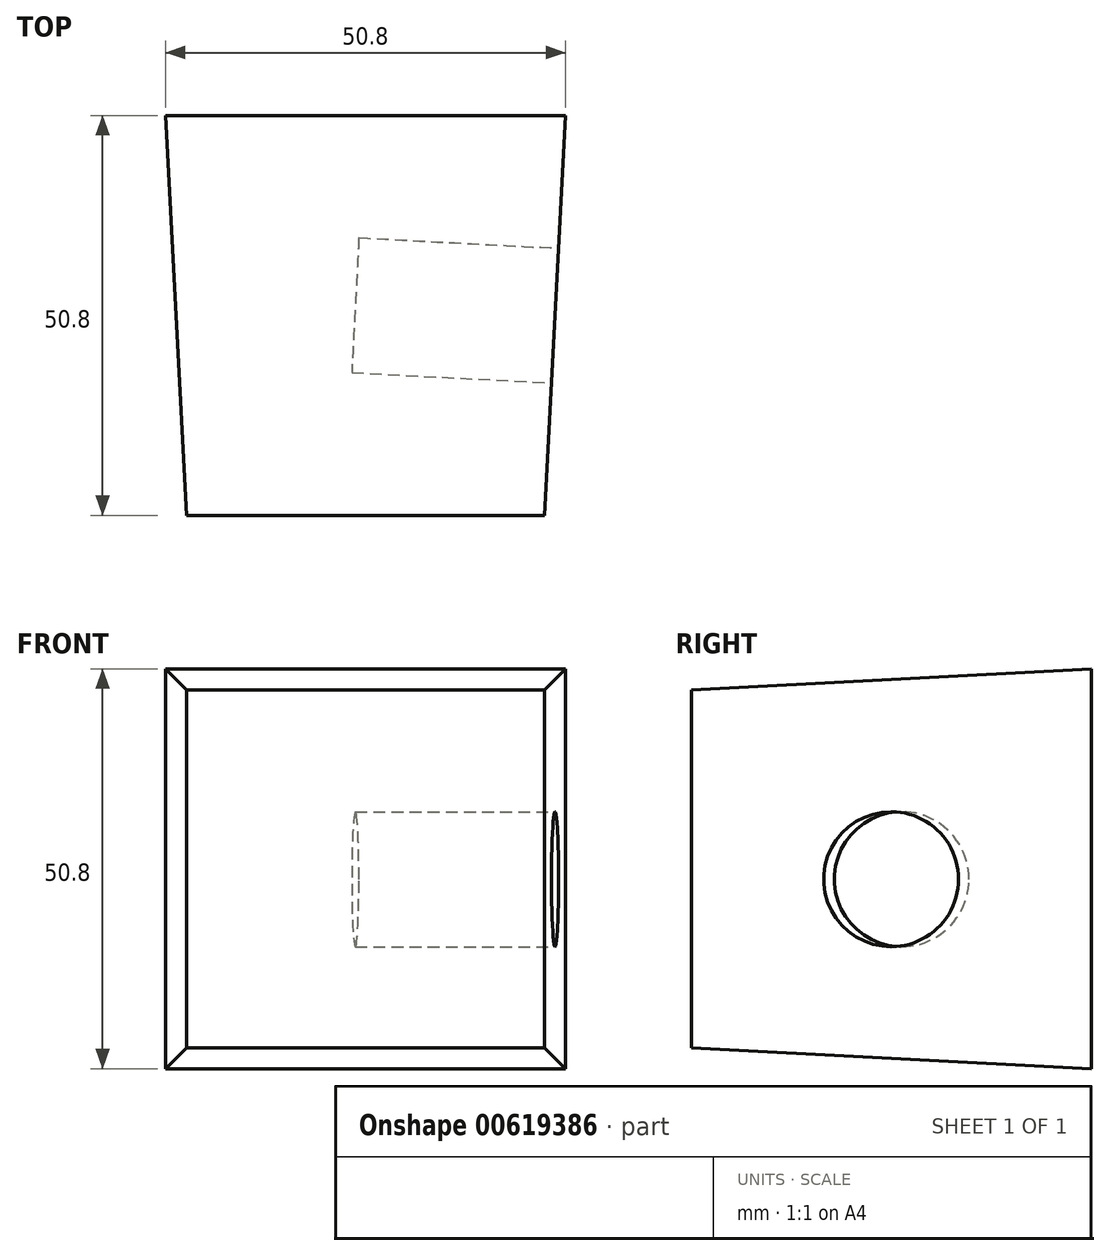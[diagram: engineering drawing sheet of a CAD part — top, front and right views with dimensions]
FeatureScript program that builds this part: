
annotation { "Feature Type Name" : "Feature", "Feature Type Description" : "" }
export const myFeature = defineFeature(function(context is Context, id is Id, definition is map)
    precondition{}
    {
        {
            var Q0;
            Q0=qCreatedBy(makeId("Front.planeOp"),FACE);
            var sketch = newSketch(context, id + "F0", { "sketchPlane" : qUnion([Q0])});
            skLineSegment(sketch, "E0", {"start": v(0, 50.8) * mm, "end": v(0, 0) * mm});
            skLineSegment(sketch, "E1", {"start": v(0, 0) * mm, "end": v(50.8, 0) * mm});
            skLineSegment(sketch, "E2", {"start": v(50.8, 0) * mm, "end": v(50.8, 50.8) * mm});
            skLineSegment(sketch, "E3", {"start": v(50.8, 50.8) * mm, "end": v(0, 50.8) * mm});
            skSolve(sketch);
        }
        {
            var Q0;
            Q0 = qSketchRegion(id + "F0", true);
            extrude(context, id + "F1", {"entities" : qUnion([Q0]), "depth" : 50.8 * mm, "offsetDistance" : 25.4 * mm, "hasDraft" : true, "draftAngle" : 3 * degree, "draftPullDirection" : true});
        }
        {
            var Q0;
            Q0=makeQuery(id+"F1.opExtrude","SWEPT_FACE",FACE,{"disambiguationData":[OSD([sQuery(id+"F0.wireOp",EDGE,"E2")])]});
            var sketch = newSketch(context, id + "F2", { "sketchPlane" : qUnion([Q0])});
            skCircle(sketch, "E4", {"center": v(-22.81, 24.07) * mm, "radius": 8.57 * mm});
            skSolve(sketch);
        }
        {
            var Q0;
            Q0 = qSketchRegion(id + "F2", true);
            extrude(context, id + "F3", {"entities" : qUnion([Q0]), "operationType" : NewBodyOperationType.REMOVE, "oppositeDirection" : true, "depth" : 25.4 * mm, "offsetDistance" : 25.4 * mm});
        }
    });
